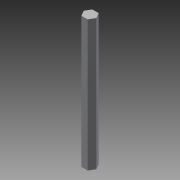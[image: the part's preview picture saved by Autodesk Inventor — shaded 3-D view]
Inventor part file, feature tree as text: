
AUTODESK INVENTOR PART (.ipt)
format: ipt  version: 2014 SP1 (Build 180222100, 222)  size: 72,192 bytes
history: native  units: in
note: dims shown in document units (in); Inventor stores cm internally (conversion verified against a paired STEP export)
features: extrude x1, sketch x1
ambient origin geometry x8: Origin, YZ Plane, XZ Plane, XY Plane, X Axis, Y Axis, Z Axis, Center Point
bodies: Solid1 (feature_tree)
feature tree (2):
  extrude  "Extrusion1"  Depth=6.0in TaperAngle=0.0deg
  sketch  "Sketch1"  dims[d0=0.5in d1=6.0in d2=0.0in]
